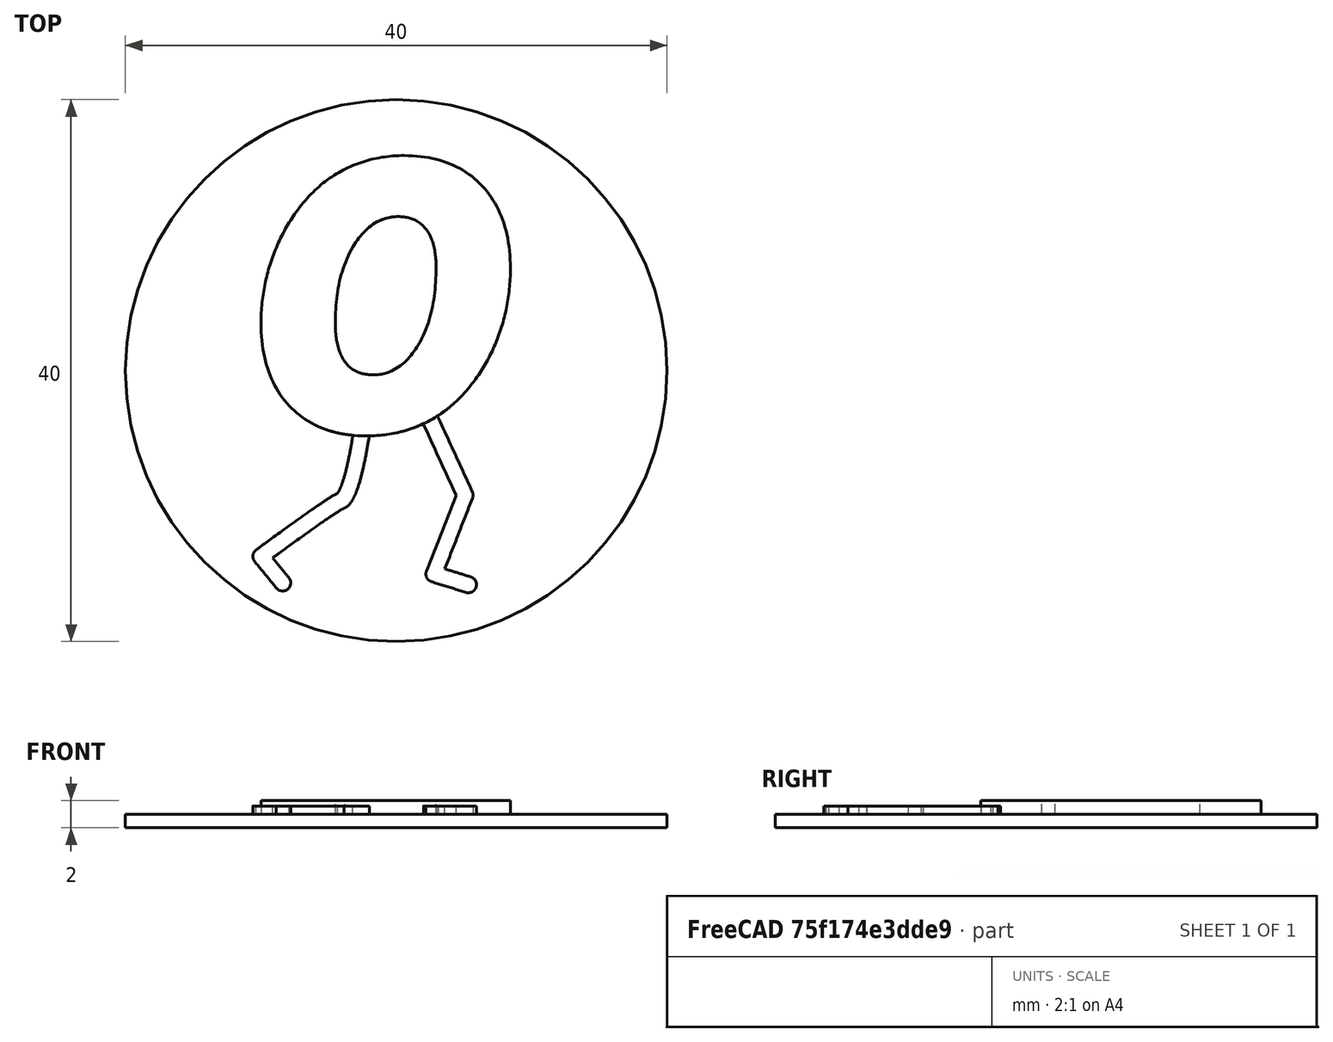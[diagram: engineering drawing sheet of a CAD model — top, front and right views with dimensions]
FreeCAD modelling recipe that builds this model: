
FCSTD DOCUMENT  (FreeCAD 0.17R12412 (Git))
Label: Bit-0-moneda
License: All rights reserved
LicenseURL: http://en.wikipedia.org/wiki/All_rights_reserved
objects: Part::Feature×4, Part::Extrusion×4, Part::MultiFuse×3, Part::Cylinder×1, Part::Cut×1
note: 13 computed .brp shape members not serialized (recipe doc carries the construction recipe); baked Part::Feature solids carry a one-line shape summary decoded from their .brp

FEATURE [Part::Feature] path6_1_7_2_6
  Placement = pos=(-20.7499,19.9057,1) rot=(0,0,1;0rad)
  shape: bbox 4.108 x 13.3 x 2e-07 mm, 0 faces, 0 solids (baked)
FEATURE [Part::Feature] path6_1_7_2_6001
  Placement = pos=(-20.7499,19.9057,1) rot=(0,0,1;0rad)
  shape: bbox 8.818 x 12.69 x 2e-07 mm, 0 faces, 0 solids (baked)
FEATURE [Part::Feature] path4641
  Placement = pos=(-20.7499,19.9057,1) rot=(0,0,1;0rad)
  shape: bbox 7.446 x 11.68 x 2.193e-07 mm, 0 faces, 0 solids (baked)
FEATURE [Part::Feature] path4641001
  Placement = pos=(-20.7499,19.9057,1) rot=(0,0,1;0rad)
  shape: bbox 18.42 x 20.69 x 2.193e-07 mm, 0 faces, 0 solids (baked)
FEATURE [Part::Cylinder] Cylinder  label="base"
  Angle = 360
  AttacherType = Attacher::AttachEngine3D
  Height = 1
  Radius = 20
FEATURE [Part::Extrusion] Extrude
  Base = -> path4641001
  Dir = (0,0,-1)
  DirMode = 2
  FaceMakerClass = Part::FaceMakerBullseye
  LengthFwd = 1
  LengthRev = 0
  Placement = pos=(0,0,1) rot=(0,0,1;0rad)
  Solid = true
  Symmetric = false
FEATURE [Part::Extrusion] Extrude001
  Base = -> path4641
  Dir = (0,0,1)
  DirMode = 2
  FaceMakerClass = Part::FaceMakerBullseye
  LengthFwd = 3
  LengthRev = 0
  Solid = true
  Symmetric = false
FEATURE [Part::Cut] Cut  label="Bit-0"
  Base = -> Extrude
  Tool = -> Extrude001
FEATURE [Part::Extrusion] Extrude002  label="right-leg"
  Base = -> path6_1_7_2_6
  Dir = (0,0,1)
  DirMode = 2
  FaceMakerClass = Part::FaceMakerBullseye
  LengthFwd = 0.6
  LengthRev = 0
  Solid = true
  Symmetric = false
FEATURE [Part::Extrusion] Extrude003  label="left-leg"
  Base = -> path6_1_7_2_6001
  Dir = (0,0,1)
  DirMode = 2
  FaceMakerClass = Part::FaceMakerBullseye
  LengthFwd = 0.6
  LengthRev = 0
  Solid = true
  Symmetric = false
FEATURE [Part::MultiFuse] Fusion  label="legs"
  Shapes = -> [Extrude002,Extrude003]
FEATURE [Part::MultiFuse] Fusion001  label="Bit-0-legs"
  Shapes = -> [Cut,Fusion]
FEATURE [Part::MultiFuse] Fusion002  label="Bit-0-coin"
  Shapes = -> [Cylinder,Fusion001]
